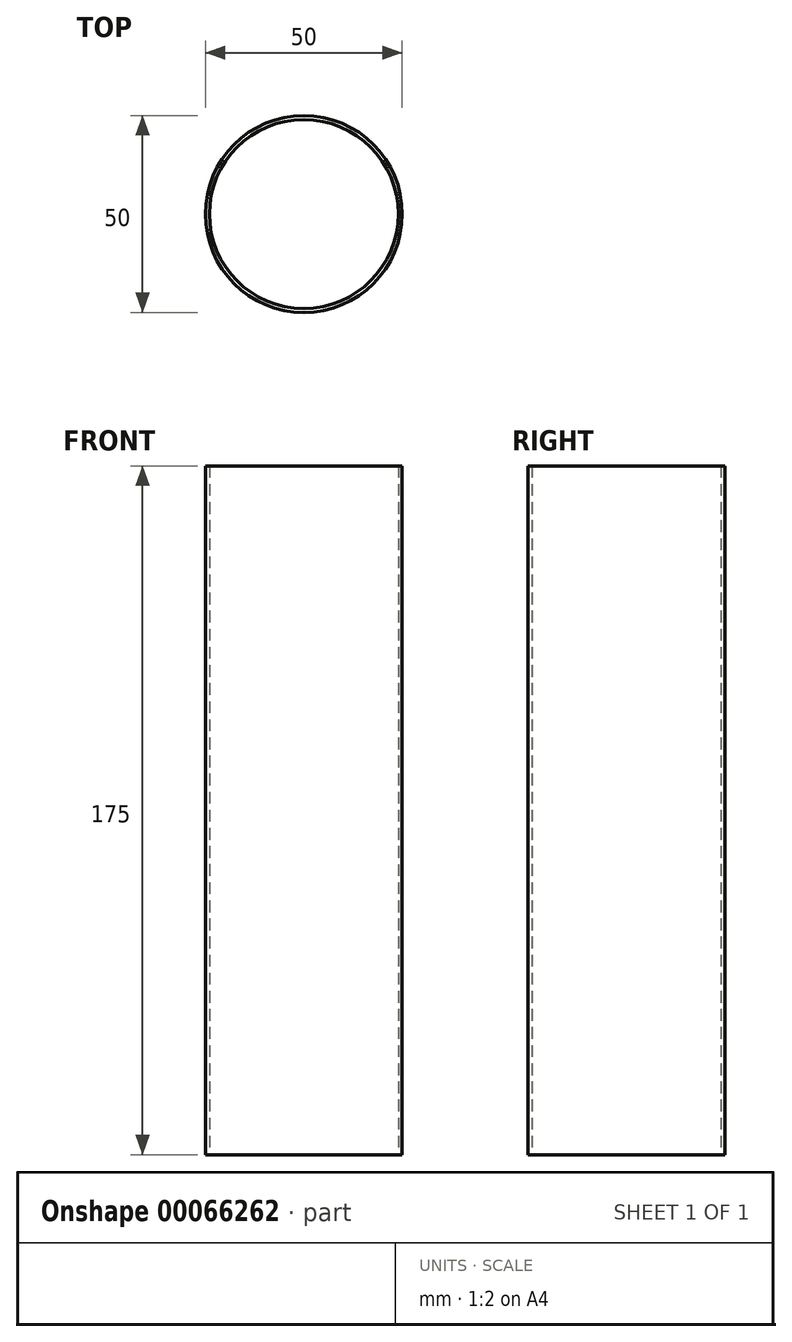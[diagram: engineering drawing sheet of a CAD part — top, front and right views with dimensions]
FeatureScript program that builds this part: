
annotation { "Feature Type Name" : "Feature", "Feature Type Description" : "" }
export const myFeature = defineFeature(function(context is Context, id is Id, definition is map)
    precondition{}
    {
        {
            var Q0;
            Q0=qCreatedBy(makeId("Top.planeOp"),FACE);
            var sketch = newSketch(context, id + "F0", { "sketchPlane" : qUnion([Q0])});
            skCircle(sketch, "E0", {"center": v(0, 0) * mm, "radius": 25 * mm});
            skCircle(sketch, "E1.0", {"center": v(0, 0) * mm, "radius": 24 * mm});
            skSolve(sketch);
        }
        {
            var Q0;
            Q0=makeQuery(id+"F0.imprint","IMPRINT",FACE,{"disambiguationData":[TD([[makeQuery(id+"F0.imprint","IMPRINT",EDGE,{"derivedFrom":sQuery(id+"F0.wireOp",EDGE,"E0")}),1.0]])]});
            extrude(context, id + "F1", {"entities" : qUnion([Q0]), "depth" : 175 * mm});
        }
    });
